FCSTD DOCUMENT  (FreeCAD 1.2R20251223 (Git shallow))
Label: modular-task-light-asm
License: All rights reserved
objects: App::Link×8, App::FeaturePython×8, App::Point×1, Assembly::JointGroup×1, Assembly::AssemblyObject×1
EXTERNAL_REF file=modular-task-light-parts.FCStd obj=Part
EXTERNAL_REF file=modular-task-light-parts.FCStd obj=Body003
EXTERNAL_REF file=modular-task-light-parts.FCStd obj=Body004
EXTERNAL_REF file=modular-task-light-parts.FCStd obj=Part001
EXTERNAL_REF file=modular-task-light-parts.FCStd obj=Part002

FEATURE [App::Point] Origin001  label="Origine"
  Role = Origin
FEATURE [App::Link] lamp_led  label="lamp-led"
  LinkPlacement = pos=(3.28e-14,181.821,89.8213) rot=(1,0,0;1.32331rad)
  LinkedObject = -> <external modular-task-light-parts.FCStd>#Part
  Placement = pos=(3.28e-14,181.821,89.8213) rot=(1,0,0;1.32331rad)
FEATURE [App::Link] Lamp_clip  label="Lamp-clip"
  LinkPlacement = pos=(3.28e-14,181.821,89.8213) rot=(1,0,0;1.32331rad)
  LinkedObject = -> <external modular-task-light-parts.FCStd>#Body003
  Placement = pos=(3.28e-14,181.821,89.8213) rot=(1,0,0;1.32331rad)
FEATURE [App::Link] Arm
  LinkPlacement = pos=(-4.2e-15,132.073,9.84695) rot=(1,0,0;0.784831rad)
  LinkedObject = -> <external modular-task-light-parts.FCStd>#Body004
  Placement = pos=(-4.2e-15,132.073,9.84695) rot=(1,0,0;0.784831rad)
FEATURE [App::FeaturePython] Joint001  label="Fixed001"  # Assembly joint (typed FeaturePython)
  Angle = 0
  AngleMax = 0
  AngleMin = 0
  Detach1 = false
  Detach2 = false
  Distance = 0
  Distance2 = 0
  EnableAngleMax = false
  EnableAngleMin = false
  EnableLengthMax = false
  EnableLengthMin = false
  JointType = 0 (Fixed)
  LengthMax = 0
  LengthMin = 0
  Placement1 = pos=(0,0,0) rot=(1,0,0;3.14159rad)
  Reference1 = -> Assembly [lamp_led.Body.Edge16,lamp_led.Body.Edge16]
  Reference2 = -> Assembly [Lamp_clip.Edge34,Lamp_clip.Edge34]
  Suppressed = false
FEATURE [App::FeaturePython] Joint  label="Revolute003"  # Assembly joint (typed FeaturePython)
  Angle = 0
  AngleMax = 0
  AngleMin = 0
  Detach1 = false
  Detach2 = false
  Distance = 0
  Distance2 = 0
  EnableAngleMax = false
  EnableAngleMin = false
  EnableLengthMax = false
  EnableLengthMin = false
  JointType = 1 (Revolute)
  LengthMax = 0
  LengthMin = 0
  Placement1 = pos=(5,-46.8,3) rot=(0.57735,0.57735,0.57735;2.0944rad)
  Placement2 = pos=(5,50,0) rot=(-0.57735,-0.57735,0.57735;2.0944rad)
  Reference1 = -> Assembly [Lamp_clip.Edge113,Lamp_clip.Edge113]
  Reference2 = -> Assembly [Arm.Edge121,Arm.Edge121]
  Suppressed = false
FEATURE [App::Link] Arm001
  LinkPlacement = pos=(-7e-16,48.3486,-12.7442) rot=(-1,0,0;0.257727rad)
  LinkedObject = -> <external modular-task-light-parts.FCStd>#Body004
  Placement = pos=(-7e-16,48.3486,-12.7442) rot=(-1,0,0;0.257727rad)
FEATURE [App::FeaturePython] Joint002  label="Revolute004"  # Assembly joint (typed FeaturePython)
  Angle = 0
  AngleMax = 0
  AngleMin = 0
  Detach1 = false
  Detach2 = false
  Distance = 0
  Distance2 = 0
  EnableAngleMax = false
  EnableAngleMin = false
  EnableLengthMax = false
  EnableLengthMin = false
  JointType = 1 (Revolute)
  LengthMax = 0
  LengthMin = 0
  Placement1 = pos=(5,-50,0) rot=(-0.57735,-0.57735,0.57735;2.0944rad)
  Placement2 = pos=(5,50,0) rot=(-0.57735,-0.57735,0.57735;2.0944rad)
  Reference1 = -> Assembly [Arm.Edge95,Arm.Edge95]
  Reference2 = -> Assembly [Arm001.Edge121,Arm001.Edge121]
  Suppressed = false
FEATURE [App::Link] Knurling_Nut_Asm  label="Knurling-Nut-Asm"
  LinkedObject = -> <external modular-task-light-parts.FCStd>#Part001
FEATURE [App::Link] Knurling_Nut_Asm001  label="Knurling-Nut-Asm001"
  LinkPlacement = pos=(-1.59e-14,96.6972,-25.4883) rot=(-1,0,0;0.257727rad)
  LinkedObject = -> <external modular-task-light-parts.FCStd>#Part001
  Placement = pos=(-1.59e-14,96.6972,-25.4883) rot=(-1,0,0;0.257727rad)
FEATURE [App::Link] Knurling_Nut_Asm002  label="Knurling-Nut-Asm002"
  LinkPlacement = pos=(4.6e-15,167.448,45.1822) rot=(1,0,0;0.784831rad)
  LinkedObject = -> <external modular-task-light-parts.FCStd>#Part001
  Placement = pos=(4.6e-15,167.448,45.1822) rot=(1,0,0;0.784831rad)
FEATURE [App::FeaturePython] Joint004  label="Fixed002"  # Assembly joint (typed FeaturePython)
  Angle = 0
  AngleMax = 0
  AngleMin = 0
  Detach1 = false
  Detach2 = false
  Distance = 0
  Distance2 = 0
  EnableAngleMax = false
  EnableAngleMin = false
  EnableLengthMax = false
  EnableLengthMin = false
  JointType = 0 (Fixed)
  LengthMax = 0
  LengthMin = 0
  Placement1 = pos=(-3.5,0,0) rot=(0.57735,0.57735,0.57735;2.0944rad)
  Placement2 = pos=(8,50,0) rot=(0.57735,0.57735,0.57735;2.0944rad)
  Reference1 = -> Assembly [Knurling_Nut_Asm002.Link.Edge254,Knurling_Nut_Asm002.Link.Edge254]
  Reference2 = -> Assembly [Arm.Edge112,Arm.Edge112]
  Suppressed = false
FEATURE [App::FeaturePython] Joint005  label="Fixed003"  # Assembly joint (typed FeaturePython)
  Angle = 0
  AngleMax = 0
  AngleMin = 0
  Detach1 = false
  Detach2 = false
  Distance = 0
  Distance2 = 0
  EnableAngleMax = false
  EnableAngleMin = false
  EnableLengthMax = false
  EnableLengthMin = false
  JointType = 0 (Fixed)
  LengthMax = 0
  LengthMin = 0
  Placement1 = pos=(-3.5,0,0) rot=(0.57735,0.57735,0.57735;2.0944rad)
  Placement2 = pos=(8,50,-3.6e-15) rot=(0.57735,0.57735,0.57735;2.0944rad)
  Reference1 = -> Assembly [Knurling_Nut_Asm001.Link.Edge254,Knurling_Nut_Asm001.Link.Edge254]
  Reference2 = -> Assembly [Arm001.Edge112,Arm001.Edge112]
  Suppressed = false
FEATURE [App::Link] _2020_Support_Asm  label="2020-Support-Asm"
  LinkedObject = -> <external modular-task-light-parts.FCStd>#Part002
FEATURE [App::FeaturePython] GroundedJoint  label="GroundedJoint003"  # Assembly grounded joint (typed FeaturePython)
  ObjectToGround = -> _2020_Support_Asm
FEATURE [App::FeaturePython] Joint006  label="Revolute007"  # Assembly joint (typed FeaturePython)
  Angle = 0
  AngleMax = 0
  AngleMin = 0
  Detach1 = false
  Detach2 = false
  Distance = 0
  Distance2 = 0
  EnableAngleMax = false
  EnableAngleMin = false
  EnableLengthMax = false
  EnableLengthMin = false
  JointType = 1 (Revolute)
  LengthMax = 0
  LengthMin = 0
  Placement1 = pos=(-5,-50,3e-15) rot=(-0.57735,-0.57735,0.57735;2.0944rad)
  Placement2 = pos=(-5,0,0) rot=(-0.57735,-0.57735,0.57735;2.0944rad)
  Reference1 = -> Assembly [Arm001.Edge1,Arm001.Edge1]
  Reference2 = -> Assembly [_2020_Support_Asm.Body005.Edge55,_2020_Support_Asm.Body005.Edge55]
  Suppressed = false
FEATURE [App::FeaturePython] Joint007  label="Fixed005"  # Assembly joint (typed FeaturePython)
  Angle = 0
  AngleMax = 0
  AngleMin = 0
  Detach1 = false
  Detach2 = false
  Distance = 0
  Distance2 = 0
  EnableAngleMax = false
  EnableAngleMin = false
  EnableLengthMax = false
  EnableLengthMin = false
  JointType = 0 (Fixed)
  LengthMax = 0
  LengthMin = 0
  Placement1 = pos=(-3.5,0,0) rot=(0.57735,0.57735,0.57735;2.0944rad)
  Placement2 = pos=(8,0,0) rot=(0.57735,0.57735,0.57735;2.0944rad)
  Reference1 = -> Assembly [Knurling_Nut_Asm.Link.Edge254,Knurling_Nut_Asm.Link.Edge254]
  Reference2 = -> Assembly [_2020_Support_Asm.Body005.Edge59,_2020_Support_Asm.Body005.Edge59]
  Suppressed = false
FEATURE [Assembly::JointGroup] Joints
  Group = -> [Joint001,Joint,Joint002,Joint004,Joint005,GroundedJoint,Joint006,Joint007]
FEATURE [Assembly::AssemblyObject] Assembly  label="modular-task-light"
  Group = -> [Joints,lamp_led,Lamp_clip,Arm,Joint001,Joint,Arm001,Joint002,Knurling_Nut_Asm,Knurling_Nut_Asm001,Knurling_Nut_Asm002,Joint004,Joint005,_2020_Support_Asm,GroundedJoint,Joint006,Joint007]
  Origin = -> Origin
  Type = Assembly

RESOLVED EXTERNAL PARTS (link-assembly join: the EXTERNAL_REF files above that resolve inside this repo's crawl, each included once):
---- part modular-task-light-parts.FCStd = doc fcstd_f716f1105b3c ----
FCSTD DOCUMENT  (FreeCAD 1.2R20251223 (Git shallow))
Label: modular-task-light-parts
License: All rights reserved
objects: Sketcher::SketchObject×27, PartDesign::Chamfer×22, PartDesign::Pocket×15, PartDesign::Pad×11, App::Point×10, PartDesign::Body×7, PartDesign::Fillet×7, Part::FeaturePython×5, App::Part×3, PartDesign::Mirrored×3, App::DocumentObjectGroup×2, PartDesign::Revolution×1, PartDesign::AdditivePipe×1, PartDesign::LinearPattern×1, PartDesign::Draft×1, PartDesign::PolarPattern×1, App::Link×1, App::VarSet×1
note: 250 computed .brp shape members not serialized (recipe doc carries the construction recipe); baked Part::Feature solids carry a one-line shape summary decoded from their .brp

FEATURE [App::Point] Origin001  label="Origine"
  Role = Origin
FEATURE [Sketcher::SketchObject] Sketch
  ArcFitTolerance = 1e-06
  AttachmentSupport = -> [Origin]
  ExternalTypes = [0]
  FullyConstrained = true
  MakeInternals = false
  MapMode = 5
  Placement = pos=(0,0,0) rot=(1,0,0;1.5708rad)
  sketch-geometry (6):
    g0: LineSegment StartX=0 StartY=0 StartZ=0 EndX=29.6 EndY=0 EndZ=0
    g1: LineSegment StartX=29.6 StartY=0 StartZ=0 EndX=29.6 EndY=7.7 EndZ=0
    g2: LineSegment StartX=29.6 StartY=7.7 StartZ=0 EndX=23.5 EndY=7.7 EndZ=0
    g3: LineSegment StartX=23.5 StartY=7.7 StartZ=0 EndX=23.5 EndY=6.2 EndZ=0
    g4: LineSegment StartX=23.5 StartY=6.2 StartZ=0 EndX=0 EndY=6.2 EndZ=0
    g5: LineSegment StartX=0 StartY=6.2 StartZ=0 EndX=0 EndY=0 EndZ=0
  constraints (17):
    c: Coincident(g-1,g0)
    c: PointOnObject(g0,g-1)
    c: Coincident(g0,g1)
    c: Vertical(g1)
    c: Coincident(g1,g2)
    c: Horizontal(g2)
    c: Coincident(g2,g3)
    c: Vertical(g3)
    c: Coincident(g3,g4)
    c: Horizontal(g4)
    c: Coincident(g4,g5)
    c: Coincident(g5,g0)
    c: Vertical(g5)
    c: DistanceX(g0,g0) = 29.6
    c: Distance(g-2,g3) = 23.5
    c: DistanceY(g1,g1) = 7.7
    c: Distance(g3,g3) = 1.5
FEATURE [PartDesign::Revolution] Revolution
  Angle = 360
  Angle2 = 0
  Axis = (0,2e-16,1)
  Base = (0,0,0)
  FuseOrder = 0
  Profile = -> Sketch
  ReferenceAxis = -> Sketch [V_Axis]
  Refine = true
  Reversed = true
  Suppressed = false
  Type = 0
FEATURE [PartDesign::Chamfer] Chamfer
  Angle = 45
  Base = -> Revolution [Edge4]
  BaseFeature = -> Revolution
  ChamferType = 0
  FlipDirection = false
  Refine = true
  Size = 1
  Size2 = 1
  SupportTransform = false
  Suppressed = false
  UseAllEdges = false
FEATURE [Sketcher::SketchObject] Sketch001
  ArcFitTolerance = 1e-06
  AttachmentSupport = -> [Origin]
  ExternalTypes = [0]
  FullyConstrained = true
  MakeInternals = false
  MapMode = 5
  sketch-geometry (3):
    g0: Circle CenterX=0 CenterY=0 CenterZ=0 NormalX=0 NormalY=0 NormalZ=1 AngleXU=0 Radius=2.25
    g1: Circle CenterX=14 CenterY=0 CenterZ=0 NormalX=0 NormalY=0 NormalZ=1 AngleXU=0 Radius=1.95
    g2: Circle CenterX=-14 CenterY=0 CenterZ=0 NormalX=0 NormalY=0 NormalZ=1 AngleXU=0 Radius=1.95
  constraints (7):
    c: Coincident(g0,g-1)
    c: PointOnObject(g1,g-1)
    c: Equal(g2,g1)
    c: Symmetric(g2,g1,g-2)
    c: Diameter(g0) = 4.5
    c: Diameter(g1) = 3.9
    c: DistanceX(g2,g1) = 28
FEATURE [PartDesign::Pocket] Pocket
  BaseFeature = -> Chamfer
  Direction = (0,0,-1)
  Length = 2
  Length2 = 5
  Profile = -> Sketch001
  ReferenceAxis = -> Sketch001 [N_Axis]
  Refine = true
  Reversed = true
  SideType = 0
  Suppressed = false
  Type = 0
  Type2 = 0
FEATURE [PartDesign::Chamfer] Chamfer001
  Angle = 45
  Base = -> Pocket [Edge2,Edge5]
  BaseFeature = -> Pocket
  ChamferType = 0
  FlipDirection = false
  Refine = true
  Size = 0.5
  Size2 = 1
  SupportTransform = false
  Suppressed = false
  UseAllEdges = false
FEATURE [Sketcher::SketchObject] Sketch002
  ArcFitTolerance = 1e-06
  AttachmentSupport = -> [Origin]
  ExternalGeometry = -> [Chamfer001]
  ExternalTypes = [0]
  FullyConstrained = true
  MakeInternals = false
  MapMode = 5
  sketch-geometry (4):
    g0: ArcOfCircle CenterX=0 CenterY=-22.1 CenterZ=0 NormalX=0 NormalY=0 NormalZ=1 AngleXU=0 Radius=2 StartAngle=-9e-16 EndAngle=3.14159
    g1: ArcOfCircle CenterX=0 CenterY=-31.1 CenterZ=0 NormalX=0 NormalY=0 NormalZ=1 AngleXU=0 Radius=2 StartAngle=3.14159 EndAngle=6.28319
    g2: LineSegment StartX=2 StartY=-22.1 StartZ=0 EndX=2 EndY=-31.1 EndZ=0
    g3: LineSegment StartX=-2 StartY=-22.1 StartZ=0 EndX=-2 EndY=-31.1 EndZ=0
  constraints (10):
    c: Tangent(g0,g2) = 1.5708
    c: Tangent(g0,g3) = -1.5708
    c: Tangent(g1,g2) = 1.5708
    c: Tangent(g1,g3) = -1.5708
    c: Equal(g0,g1)
    c: PointOnObject(g0,g-2)
    c: PointOnObject(g1,g-2)
    c: Distance(g1,g1) = 4
    c: Distance(g0,g-3) = 7
    c: Tangent(g1,g-3)
FEATURE [PartDesign::Pocket] Pocket001
  BaseFeature = -> Chamfer001
  Direction = (0,0,-1)
  Length = 3
  Length2 = 5
  Profile = -> Sketch002
  ReferenceAxis = -> Sketch002 [N_Axis]
  Refine = true
  Reversed = true
  SideType = 0
  Suppressed = false
  Type = 0
  Type2 = 0
FEATURE [PartDesign::Body] Body  label="lamp-led-body"
  AllowCompound = true
  Group = -> [Sketch,Revolution,Chamfer,Sketch001,Pocket,Chamfer001,Sketch002,Pocket001]
  Origin = -> Origin
  Tip = -> Pocket001
FEATURE [App::Point] Origin003  label="Origine002"
  Role = Origin
FEATURE [Sketcher::SketchObject] Sketch003
  ArcFitTolerance = 1e-06
  AttachmentSupport = -> [Origin002]
  ExternalTypes = [0]
  FullyConstrained = true
  MakeInternals = false
  MapMode = 5
  sketch-geometry (1):
    g0: Circle CenterX=0 CenterY=0 CenterZ=0 NormalX=0 NormalY=0 NormalZ=1 AngleXU=0 Radius=25
  constraints (2):
    c: Coincident(g0,g-1)
    c: Diameter(g0) = 50
FEATURE [PartDesign::Pad] Pad
  Direction = (0,0,1)
  Length = 1
  Length2 = 10
  Profile = -> Sketch003
  ReferenceAxis = -> Sketch003 [N_Axis]
  Refine = true
  SideType = 0
  Suppressed = false
  Type = 0
  Type2 = 0
FEATURE [PartDesign::Body] Body001  label="lamp-led-diffuser"
  AllowCompound = true
  Group = -> [Sketch003,Pad]
  Origin = -> Origin002
  Placement = pos=(-9e-16,2.7e-15,5.45) rot=(0,0,1;3.14159rad)
  Tip = -> Pad
FEATURE [App::Point] Origin005  label="Origine004"
  Role = Origin
FEATURE [Sketcher::SketchObject] Sketch004
  ArcFitTolerance = 1e-06
  AttachmentSupport = -> [Origin004]
  ExternalTypes = [0]
  FullyConstrained = true
  MakeInternals = false
  MapMode = 5
  Placement = pos=(0,0,0) rot=(1,0,0;1.5708rad)
  sketch-geometry (1):
    g0: Circle CenterX=0 CenterY=0 CenterZ=0 NormalX=0 NormalY=0 NormalZ=1 AngleXU=0 Radius=1.475
  constraints (2):
    c: Coincident(g0,g-1)
    c: Diameter(g0) = 2.95
FEATURE [PartDesign::Pad] Pad001
  Direction = (0,-1,2e-16)
  Length = 15
  Length2 = 10
  Profile = -> Sketch004
  ReferenceAxis = -> Sketch004 [N_Axis]
  Refine = true
  SideType = 0
  Suppressed = false
  Type = 0
  Type2 = 0
FEATURE [PartDesign::Body] Body002  label="lamp-led-cable"
  AllowCompound = true
  Group = -> [Sketch004,Pad001]
  Origin = -> Origin004
  Placement = pos=(0,-20,1.5) rot=(0,0,1;0rad)
  Tip = -> Pad001
FEATURE [App::Part] Part  label="lamp-led"
  Group = -> [Body,Body001,Body002]
  Origin = -> Origin006
FEATURE [App::Point] Origin007  label="Origine006"
  Role = Origin
FEATURE [App::Point] Origin009  label="Origine008"
  Role = Origin
FEATURE [Sketcher::SketchObject] Sketch005
  ArcFitTolerance = 1e-06
  AttachmentSupport = -> [Origin008]
  ExternalTypes = [0]
  FullyConstrained = true
  MakeInternals = false
  MapMode = 5
  sketch-geometry (2):
    g0: Circle CenterX=0 CenterY=0 CenterZ=0 NormalX=0 NormalY=0 NormalZ=1 AngleXU=0 Radius=29.8
    g1: Circle CenterX=0 CenterY=0 CenterZ=0 NormalX=0 NormalY=0 NormalZ=1 AngleXU=0 Radius=31.8
  constraints (4):
    c: Coincident(g0,g-1)
    c: Diameter(g0) = 59.6
    c: Coincident(g1,g0)
    c: Distance(g0,g1) = 2
FEATURE [PartDesign::Pad] Pad002
  Direction = (0,0,1)
  Length = 8
  Length2 = 10
  Profile = -> Sketch005
  ReferenceAxis = -> Sketch005 [N_Axis]
  Refine = true
  SideType = 0
  Suppressed = false
  Type = 0
  Type2 = 0
FEATURE [Sketcher::SketchObject] Sketch008
  ArcFitTolerance = 1e-06
  AttachmentSupport = -> [Origin008]
  ExternalGeometry = -> [Pad002]
  ExternalTypes = [0]
  FullyConstrained = true
  MakeInternals = false
  MapMode = 5
  sketch-geometry (1):
    g0: Circle CenterX=0 CenterY=0 CenterZ=0 NormalX=0 NormalY=0 NormalZ=1 AngleXU=0 Radius=31.8
  constraints (2):
    c: Coincident(g0,g-1)
    c: Equal(g-3,g0)
FEATURE [PartDesign::Pad] Pad003
  BaseFeature = -> Pad002
  Direction = (0,0,1)
  Length = 2
  Length2 = 10
  Profile = -> Sketch008
  ReferenceAxis = -> Sketch008 [N_Axis]
  Refine = true
  Reversed = true
  SideType = 0
  Suppressed = false
  Type = 0
  Type2 = 0
FEATURE [Sketcher::SketchObject] Sketch009
  ArcFitTolerance = 1e-06
  AttachmentSupport = -> [Origin008]
  ExternalTypes = [0]
  FullyConstrained = true
  MakeInternals = false
  MapMode = 5
  Placement = pos=(0,0,0) rot=(0.57735,0.57735,0.57735;2.0944rad)
  sketch-geometry (8):
    g0: LineSegment StartX=-7 StartY=0 StartZ=0 EndX=-5 EndY=0 EndZ=0
    g1: LineSegment StartX=-5 StartY=0 StartZ=0 EndX=-5 EndY=10 EndZ=0
    g2: LineSegment StartX=-5 StartY=10 StartZ=0 EndX=-7 EndY=10 EndZ=0
    g3: LineSegment StartX=-7 StartY=10 StartZ=0 EndX=-7 EndY=0 EndZ=0
    g4: LineSegment StartX=5 StartY=0 StartZ=0 EndX=7 EndY=0 EndZ=0
    g5: LineSegment StartX=7 StartY=0 StartZ=0 EndX=7 EndY=10 EndZ=0
    g6: LineSegment StartX=7 StartY=10 StartZ=0 EndX=5 EndY=10 EndZ=0
    g7: LineSegment StartX=5 StartY=10 StartZ=0 EndX=5 EndY=0 EndZ=0
  constraints (23):
    c: Coincident(g0,g1)
    c: Coincident(g1,g2)
    c: Coincident(g2,g3)
    c: Coincident(g3,g0)
    c: Horizontal(g0)
    c: Horizontal(g2)
    c: Vertical(g1)
    c: Vertical(g3)
    c: PointOnObject(g0,g-1)
    c: Coincident(g4,g5)
    c: Coincident(g5,g6)
    c: Coincident(g6,g7)
    c: Coincident(g7,g4)
    c: Horizontal(g4)
    c: Horizontal(g6)
    c: Vertical(g5)
    c: Vertical(g7)
    c: PointOnObject(g4,g-1)
    c: Equal(g6,g2)
    c: Symmetric(g1,g6,g-2)
    c: Distance(g6,g6) = 2
    c: Distance(g1,g6) = 10
    c: Distance(g5,g5) = 10
FEATURE [PartDesign::Pocket] Pocket003
  BaseFeature = -> Pad003
  Direction = (-1,0,0)
  Length = 5
  Length2 = 5
  Profile = -> Sketch009
  ReferenceAxis = -> Sketch009 [N_Axis]
  Refine = true
  SideType = 2
  Suppressed = false
  Type = 1
  Type2 = 0
FEATURE [PartDesign::Pad] Pad004
  BaseFeature = -> Pocket003
  Direction = (0,0,1)
  Length = 1
  Length2 = 10
  Profile = -> Pocket003 [Face10,Face1]
  Refine = true
  SideType = 0
  Suppressed = false
  Type = 0
  Type2 = 0
FEATURE [Sketcher::SketchObject] Sketch010
  ArcFitTolerance = 1e-06
  AttachmentSupport = -> [Pad004]
  ExternalTypes = [0,0]
  FullyConstrained = true
  MakeInternals = false
  MapMode = 5
  Placement = pos=(0,5,0) rot=(0,0.707107,0.707107;3.14159rad)
  sketch-geometry (4):
    g0: LineSegment StartX=29.3775 StartY=9 StartZ=0 EndX=28.3775 EndY=9 EndZ=0
    g1: LineSegment StartX=28.3775 StartY=9 StartZ=0 EndX=28.3775 EndY=8 EndZ=0
    g2: LineSegment StartX=28.3775 StartY=8 StartZ=0 EndX=29.3775 EndY=7.2 EndZ=0
    g3: LineSegment StartX=29.3775 StartY=7.2 StartZ=0 EndX=29.3775 EndY=9 EndZ=0
  constraints (12):
    c: Horizontal(g0)
    c: Coincident(g0,g1)
    c: Vertical(g1)
    c: Coincident(g1,g2)
    c: PointOnObject(g2,g-3)
    c: Coincident(g2,g3)
    c: Coincident(g3,g0)
    c: DistanceX(g0,g0) = 1
    c: DistanceY(g1,g1) = 1
    c: DistanceY(g3,g3) = 1.8
    c: PointOnObject(g0,g-3)
    c: Distance(g-1,g0) = 9
FEATURE [PartDesign::AdditivePipe] AdditivePipe
  AuxiliaryCurvilinear = true
  AuxiliarySpineTangent = false
  BaseFeature = -> Pad004
  Binormal = (0,0,0)
  Mode = 1
  Profile = -> Sketch010
  Refine = true
  Spine = -> Pad004 [Edge2]
  SpineTangent = false
  Suppressed = false
  Transformation = 0
  Transition = 0
FEATURE [Sketcher::SketchObject] Sketch011
  ArcFitTolerance = 1e-06
  AttachmentSupport = -> [Origin008]
  ExternalGeometry = -> [AdditivePipe]
  ExternalTypes = [0]
  FullyConstrained = true
  MakeInternals = false
  MapMode = 5
  Placement = pos=(0,0,0) rot=(1,0,0;1.5708rad)
  sketch-geometry (5):
    g0: LineSegment StartX=0 StartY=0 StartZ=0 EndX=-30.3 EndY=0 EndZ=0
    g1: LineSegment StartX=-30.3 StartY=0 StartZ=0 EndX=-30.3 EndY=1 EndZ=0
    g2: LineSegment StartX=-30.3 StartY=1 StartZ=0 EndX=-27.3 EndY=4 EndZ=0
    g3: LineSegment StartX=-27.3 StartY=4 StartZ=0 EndX=0 EndY=4 EndZ=0
    g4: LineSegment StartX=0 StartY=4 StartZ=0 EndX=0 EndY=0 EndZ=0
  constraints (14):
    c: Coincident(g-1,g0)
    c: PointOnObject(g0,g-1)
    c: Coincident(g0,g1)
    c: Vertical(g1)
    c: Coincident(g1,g2)
    c: Coincident(g2,g3)
    c: Horizontal(g3)
    c: Coincident(g3,g4)
    c: Coincident(g4,g0)
    c: Vertical(g4)
    c: Distance(g1,g1) = 1
    c: Distance(g4,g4) = 4
    c: Angle(g2,g1) = 0.785398
    c: Distance(g-3,g1) = 1.5
FEATURE [PartDesign::Pocket] Pocket004
  BaseFeature = -> AdditivePipe
  Direction = (0,1,-2e-16)
  Length = 11
  Length2 = 5
  Profile = -> Sketch011
  ReferenceAxis = -> Sketch011 [N_Axis]
  Refine = true
  SideType = 2
  Suppressed = false
  Type = 0
  Type2 = 0
FEATURE [PartDesign::Mirrored] Mirrored
  BaseFeature = -> Pocket004
  MirrorPlane = -> Sketch011 [V_Axis]
  Originals = -> [Pocket004,AdditivePipe]
  Refine = true
  Suppressed = false
  TransformMode = 0
FEATURE [PartDesign::Fillet] Fillet
  Base = -> Mirrored [Edge1,Edge3,Edge69,Edge57]
  BaseFeature = -> Mirrored
  Radius = 0.4
  Refine = true
  SupportTransform = false
  Suppressed = false
  UseAllEdges = false
FEATURE [PartDesign::Fillet] Fillet001
  Base = -> Fillet [Edge77,Edge58,Edge55,Edge80]
  BaseFeature = -> Fillet
  Radius = 2
  Refine = true
  SupportTransform = false
  Suppressed = false
  UseAllEdges = false
FEATURE [PartDesign::Chamfer] Chamfer002
  Angle = 45
  Base = -> Fillet001 [Edge21,Edge7]
  BaseFeature = -> Fillet001
  ChamferType = 0
  FlipDirection = false
  Refine = true
  Size = 1
  Size2 = 1
  SupportTransform = false
  Suppressed = false
  UseAllEdges = false
FEATURE [PartDesign::Fillet] Fillet003
  Base = -> Chamfer002 [Edge39,Edge41,Edge45,Edge28]
  BaseFeature = -> Chamfer002
  Radius = 1
  Refine = true
  SupportTransform = false
  Suppressed = false
  UseAllEdges = false
FEATURE [Sketcher::SketchObject] Sketch012
  ArcFitTolerance = 1e-06
  AttachmentSupport = -> [Origin008]
  ExternalTypes = [0]
  FullyConstrained = true
  MakeInternals = false
  MapMode = 5
  sketch-geometry (4):
    g0: LineSegment StartX=-5 StartY=-31.4045 StartZ=0 EndX=-5 EndY=-51.8 EndZ=0
    g1: LineSegment StartX=-5 StartY=-51.8 StartZ=0 EndX=5 EndY=-51.8 EndZ=0
    g2: LineSegment StartX=5 StartY=-51.8 StartZ=0 EndX=5 EndY=-31.4045 EndZ=0
    g3: LineSegment StartX=5 StartY=-31.4045 StartZ=0 EndX=-5 EndY=-31.4045 EndZ=0
  constraints (12):
    c: Coincident(g0,g1)
    c: Coincident(g1,g2)
    c: Coincident(g2,g3)
    c: Coincident(g3,g0)
    c: Vertical(g0)
    c: Vertical(g2)
    c: Horizontal(g1)
    c: Horizontal(g3)
    c: PointOnObject(g0,g-3)
    c: PointOnObject(g2,g-3)
    c: Distance(g1,g1) = 10
    c: Distance(g-3,g1) = 20
FEATURE [PartDesign::Pad] Pad005
  BaseFeature = -> Fillet003
  Direction = (0,0,1)
  Length = 8
  Length2 = 2
  Profile = -> Sketch012
  ReferenceAxis = -> Sketch012 [N_Axis]
  Refine = true
  SideType = 1
  Suppressed = false
  Type = 0
  Type2 = 0
FEATURE [PartDesign::Fillet] Fillet004
  Base = -> Pad005 [Edge115]
  BaseFeature = -> Pad005
  Radius = 5
  Refine = true
  SupportTransform = false
  Suppressed = false
  UseAllEdges = false
FEATURE [PartDesign::Chamfer] Chamfer003
  Angle = 45
  Base = -> Fillet004 [Edge51]
  BaseFeature = -> Fillet004
  ChamferType = 0
  FlipDirection = false
  Refine = true
  Size = 1
  Size2 = 1
  SupportTransform = false
  Suppressed = false
  UseAllEdges = false
FEATURE [PartDesign::Fillet] Fillet005
  Base = -> Chamfer003 [Edge47,Edge6]
  BaseFeature = -> Chamfer003
  Radius = 2
  Refine = true
  SupportTransform = false
  Suppressed = false
  UseAllEdges = false
FEATURE [Sketcher::SketchObject] Sketch013
  ArcFitTolerance = 1e-06
  AttachmentSupport = -> [Origin008]
  ExternalTypes = [0]
  FullyConstrained = true
  MakeInternals = false
  MapMode = 5
  sketch-geometry (1):
    g0: Circle CenterX=0 CenterY=0 CenterZ=0 NormalX=0 NormalY=0 NormalZ=1 AngleXU=0 Radius=25
  constraints (2):
    c: Coincident(g0,g-1)
    c: Diameter(g0) = 50
FEATURE [PartDesign::Pocket] Pocket005
  BaseFeature = -> Fillet005
  Direction = (0,0,-1)
  Length = 5
  Length2 = 5
  Profile = -> Sketch013
  ReferenceAxis = -> Sketch013 [N_Axis]
  Refine = true
  SideType = 0
  Suppressed = false
  Type = 0
  Type2 = 0
FEATURE [Sketcher::SketchObject] Sketch014
  ArcFitTolerance = 1e-06
  AttachmentSupport = -> [Origin008]
  ExternalGeometry = -> [Pocket005]
  ExternalTypes = [0]
  FullyConstrained = true
  MakeInternals = false
  MapMode = 5
  Placement = pos=(0,0,0) rot=(1,0,0;1.5708rad)
  sketch-geometry (6):
    g0: ArcOfCircle CenterX=0 CenterY=-1.32361 CenterZ=0 NormalX=0 NormalY=0 NormalZ=1 AngleXU=0 Radius=1.6 StartAngle=3.14159 EndAngle=6.28319
    g1: ArcOfCircle CenterX=0 CenterY=1.5 CenterZ=0 NormalX=0 NormalY=0 NormalZ=1 AngleXU=0 Radius=1.6 StartAngle=0 EndAngle=3.14159
    g2: LineSegment StartX=-1.6 StartY=-1.32361 StartZ=0 EndX=-1.6 EndY=1.5 EndZ=0
    g3: LineSegment StartX=1.6 StartY=-1.32361 StartZ=0 EndX=1.6 EndY=1.5 EndZ=0
    g4: GeomPoint X=1.45 Y=-2 Z=0
    g5: GeomPoint X=-1.45 Y=-2 Z=0
  constraints (15):
    c: Tangent(g0,g2) = 1.5708
    c: Tangent(g0,g3) = -1.5708
    c: Tangent(g1,g2) = 1.5708
    c: Tangent(g1,g3) = -1.5708
    c: Equal(g0,g1)
    c: PointOnObject(g0,g-2)
    c: PointOnObject(g1,g-2)
    c: Distance(g1,g-1) = 1.5
    c: Distance(g1,g1) = 3.2
    c: PointOnObject(g4,g-3)
    c: PointOnObject(g5,g-3)
    c: PointOnObject(g4,g0)
    c: PointOnObject(g5,g0)
    c: Distance(g5,g4) = 2.9
    c: Distance(g1,g-3) = 3.5
FEATURE [PartDesign::Pocket] Pocket006
  BaseFeature = -> Pocket005
  Direction = (0,1,-2e-16)
  Length = 5
  Length2 = 5
  Profile = -> Sketch014
  ReferenceAxis = -> Sketch014 [N_Axis]
  Refine = true
  Reversed = true
  SideType = 0
  Suppressed = false
  Type = 1
  Type2 = 0
FEATURE [Sketcher::SketchObject] Sketch015
  ArcFitTolerance = 1e-06
  AttachmentSupport = -> [Origin008]
  ExternalGeometry = -> [Pocket006]
  ExternalTypes = [0]
  FullyConstrained = true
  MakeInternals = false
  MapMode = 5
  Placement = pos=(0,0,0) rot=(0.57735,0.57735,0.57735;2.0944rad)
  sketch-geometry (2):
    g0: Circle CenterX=-46.8 CenterY=3 CenterZ=0 NormalX=0 NormalY=0 NormalZ=1 AngleXU=0 Radius=2.5
    g1: Circle [constr] CenterX=-46.8 CenterY=3 CenterZ=0 NormalX=0 NormalY=0 NormalZ=1 AngleXU=0 Radius=1.7
  constraints (4):
    c: Coincident(g0,g-3)
    c: Coincident(g1,g0)
    c: Diameter(g1) = 3.4
    c: Distance(g1,g0) = 0.8
FEATURE [PartDesign::Pad] Pad006
  BaseFeature = -> Pocket006
  Direction = (1,0,0)
  Length = 10
  Length2 = 10
  Profile = -> Sketch015
  ReferenceAxis = -> Sketch015 [N_Axis]
  Refine = true
  SideType = 2
  Suppressed = false
  Type = 0
  Type2 = 0
FEATURE [Sketcher::SketchObject] Sketch016
  ArcFitTolerance = 1e-06
  AttachmentSupport = -> [Origin008]
  ExternalGeometry = -> [Pad006]
  ExternalTypes = [0]
  FullyConstrained = true
  MakeInternals = false
  MapMode = 5
  Placement = pos=(0,0,0) rot=(0.57735,0.57735,0.57735;2.0944rad)
  sketch-geometry (1):
    g0: Circle CenterX=-46.8 CenterY=3 CenterZ=0 NormalX=0 NormalY=0 NormalZ=1 AngleXU=0 Radius=1.7
  constraints (2):
    c: Coincident(g0,g-3)
    c: Diameter(g0) = 3.4
FEATURE [PartDesign::Pocket] Pocket007
  BaseFeature = -> Pad006
  Direction = (-1,0,0)
  Length = 5
  Length2 = 5
  Profile = -> Sketch016
  ReferenceAxis = -> Sketch016 [N_Axis]
  Refine = true
  SideType = 2
  Suppressed = false
  Type = 1
  Type2 = 0
FEATURE [PartDesign::Chamfer] Chamfer004
  Angle = 45
  Base = -> Pocket007 [Edge68,Edge49]
  BaseFeature = -> Pocket007
  ChamferType = 0
  FlipDirection = false
  Refine = true
  Size = 0.6
  Size2 = 1
  SupportTransform = false
  Suppressed = false
  UseAllEdges = false
FEATURE [PartDesign::Fillet] Fillet006
  Base = -> Chamfer004 [Edge70,Edge72]
  BaseFeature = -> Chamfer004
  Radius = 3
  Refine = true
  SupportTransform = false
  Suppressed = false
  UseAllEdges = false
FEATURE [PartDesign::Chamfer] Chamfer005
  Angle = 45
  Base = -> Fillet006 [Edge14]
  BaseFeature = -> Fillet006
  ChamferType = 0
  FlipDirection = false
  Refine = true
  Size = 0.8
  Size2 = 1
  SupportTransform = false
  Suppressed = false
  UseAllEdges = false
FEATURE [PartDesign::Body] Body003  label="Lamp-clip"
  AllowCompound = true
  Group = -> [Sketch005,Pad002,Sketch008,Pad003,Sketch009,Pocket003,Pad004,Sketch010,AdditivePipe,Sketch011,Pocket004,Mirrored,Fillet,Fillet001,Chamfer002,Fillet003,Sketch012,Pad005,Fillet004,Chamfer003,Fillet005,Sketch013,Pocket005,Sketch014,Pocket006,Sketch015,Pad006,Sketch016,Pocket007,Chamfer004,Fillet006,Chamfer005]
  Origin = -> Origin008
  Tip = -> Chamfer005
FEATURE [App::Point] Origin011  label="Origine010"
  Role = Origin
FEATURE [Sketcher::SketchObject] Sketch017
  ArcFitTolerance = 1e-06
  AttachmentSupport = -> [Origin010]
  ExternalTypes = [0]
  FullyConstrained = true
  MakeInternals = false
  MapMode = 5
  Placement = pos=(0,0,0) rot=(0.57735,0.57735,0.57735;2.0944rad)
  expr: Constraints[10] = VarSet.arm_length
  sketch-geometry (8):
    g0: LineSegment StartX=-55 StartY=0 StartZ=0 EndX=-55 EndY=-5 EndZ=0
    g1: LineSegment StartX=-55 StartY=-5 StartZ=0 EndX=55 EndY=-5 EndZ=0
    g2: LineSegment StartX=55 StartY=-5 StartZ=0 EndX=55 EndY=0 EndZ=0
    g3: ArcOfCircle CenterX=-50 CenterY=0 CenterZ=0 NormalX=0 NormalY=0 NormalZ=1 AngleXU=0 Radius=5 StartAngle=1.5708 EndAngle=3.14159
    g4: ArcOfCircle CenterX=50 CenterY=0 CenterZ=0 NormalX=0 NormalY=0 NormalZ=1 AngleXU=0 Radius=5 StartAngle=0 EndAngle=1.5708
    g5: LineSegment StartX=50 StartY=5 StartZ=0 EndX=-50 EndY=5 EndZ=0
    g6: Circle CenterX=50 CenterY=0 CenterZ=0 NormalX=0 NormalY=0 NormalZ=1 AngleXU=0 Radius=1.7
    g7: Circle CenterX=-50 CenterY=0 CenterZ=0 NormalX=0 NormalY=0 NormalZ=1 AngleXU=0 Radius=1.7
  constraints (20):
    c: PointOnObject(g0,g-1)
    c: Vertical(g0)
    c: Coincident(g0,g1)
    c: Horizontal(g1)
    c: Coincident(g1,g2)
    c: PointOnObject(g3,g-1)
    c: Coincident(g3,g0)
    c: Horizontal(g5)
    c: Tangent(g3,g1)
    c: Distance(g4,g1) = 10
    c: DistanceX(g3,g4) = 100
    c: Coincident(g6,g4)
    c: Coincident(g7,g3)
    c: Tangent(g5,g3) = -1.5708
    c: Equal(g6,g7)
    c: Diameter(g7) = 3.4
    c: Tangent(g4,g2) = -1.5708
    c: Vertical(g2)
    c: Tangent(g5,g4) = -1.5708
    c: Symmetric(g4,g3,g-2)
FEATURE [PartDesign::Pad] Pad007
  Direction = (1,0,0)
  Length = 16
  Length2 = 10
  Profile = -> Sketch017
  ReferenceAxis = -> Sketch017 [N_Axis]
  Refine = true
  SideType = 2
  Suppressed = false
  Type = 0
  Type2 = 0
FEATURE [Sketcher::SketchObject] Sketch018
  ArcFitTolerance = 1e-06
  AttachmentSupport = -> [Origin010]
  ExternalGeometry = -> [Pad007]
  ExternalTypes = [0,0]
  FullyConstrained = true
  MakeInternals = false
  MapMode = 5
  Placement = pos=(0,0,0) rot=(0.57735,0.57735,0.57735;2.0944rad)
  sketch-geometry (5):
    g0: LineSegment StartX=42.5 StartY=-5 StartZ=0 EndX=57.5 EndY=-5 EndZ=0
    g1: LineSegment StartX=57.5 StartY=-5 StartZ=0 EndX=57.5 EndY=5 EndZ=0
    g2: LineSegment StartX=57.5 StartY=5 StartZ=0 EndX=42.5 EndY=5 EndZ=0
    g3: LineSegment StartX=42.5 StartY=5 StartZ=0 EndX=42.5 EndY=-5 EndZ=0
    g4: GeomPoint [constr] X=50 Y=0 Z=0
  constraints (12):
    c: Coincident(g0,g1)
    c: Coincident(g1,g2)
    c: Coincident(g2,g3)
    c: Coincident(g3,g0)
    c: Horizontal(g0)
    c: Horizontal(g2)
    c: Vertical(g1)
    c: Vertical(g3)
    c: Symmetric(g2,g0,g4)
    c: Coincident(g4,g-3)
    c: PointOnObject(g2,g-4)
    c: DistanceX(g2,g2) = 15
FEATURE [PartDesign::Pocket] Pocket008
  BaseFeature = -> Pad007
  Direction = (-1,0,0)
  Length = 10
  Length2 = 5
  Profile = -> Sketch018
  ReferenceAxis = -> Sketch018 [N_Axis]
  Refine = true
  SideType = 2
  Suppressed = false
  Type = 0
  Type2 = 0
FEATURE [PartDesign::Chamfer] Chamfer006
  Angle = 45
  Base = -> Pocket008 [Edge9,Edge13]
  BaseFeature = -> Pocket008
  ChamferType = 0
  FlipDirection = false
  Refine = true
  Size = 2
  Size2 = 1
  SupportTransform = false
  Suppressed = false
  UseAllEdges = false
FEATURE [Sketcher::SketchObject] Sketch019
  ArcFitTolerance = 1e-06
  AttachmentSupport = -> [Origin010]
  ExternalTypes = [0]
  FullyConstrained = true
  MakeInternals = false
  MapMode = 5
  Placement = pos=(0,0,0) rot=(1,0,0;1.5708rad)
  sketch-geometry (4):
    g0: ArcOfCircle CenterX=0 CenterY=-5 CenterZ=0 NormalX=0 NormalY=0 NormalZ=1 AngleXU=0 Radius=1.7 StartAngle=3.14159 EndAngle=6.28319
    g1: ArcOfCircle CenterX=0 CenterY=-1.5 CenterZ=0 NormalX=0 NormalY=0 NormalZ=1 AngleXU=0 Radius=1.7 StartAngle=-6.87637e-11 EndAngle=3.14159
    g2: LineSegment StartX=-1.7 StartY=-5 StartZ=0 EndX=-1.7 EndY=-1.5 EndZ=0
    g3: LineSegment StartX=1.7 StartY=-5 StartZ=0 EndX=1.7 EndY=-1.5 EndZ=0
  constraints (10):
    c: Tangent(g0,g2) = 1.5708
    c: Tangent(g0,g3) = -1.5708
    c: Tangent(g1,g2) = 1.5708
    c: Tangent(g1,g3) = -1.5708
    c: Equal(g0,g1)
    c: PointOnObject(g1,g-2)
    c: PointOnObject(g0,g-2)
    c: PointOnObject(g0,g-3)
    c: Distance(g1,g1) = 3.4
    c: DistanceY(g3,g3) = 3.5
FEATURE [PartDesign::Pocket] Pocket009
  BaseFeature = -> Chamfer006
  Direction = (0,1,-2e-16)
  Length = 5
  Length2 = 5
  Profile = -> Sketch019
  ReferenceAxis = -> Sketch019 [N_Axis]
  Refine = true
  SideType = 2
  Suppressed = false
  Type = 1
  Type2 = 0
FEATURE [Sketcher::SketchObject] Sketch020
  ArcFitTolerance = 1e-06
  AttachmentSupport = -> [Origin010]
  ExternalGeometry = -> [Pocket009]
  ExternalTypes = [0,0]
  FullyConstrained = true
  MakeInternals = false
  MapMode = 5
  Placement = pos=(0,0,0) rot=(1,0,0;1.5708rad)
  sketch-geometry (6):
    g0: LineSegment StartX=-1.7 StartY=-5 StartZ=0 EndX=-1.4 EndY=-5 EndZ=0
    g1: LineSegment StartX=-1.7 StartY=-5 StartZ=0 EndX=-1.7 EndY=-4 EndZ=0
    g2: LineSegment StartX=-1.7 StartY=-4 StartZ=0 EndX=-1.4 EndY=-5 EndZ=0
    g3: LineSegment StartX=1.7 StartY=-5 StartZ=0 EndX=1.4 EndY=-5 EndZ=0
    g4: LineSegment StartX=1.4 StartY=-5 StartZ=0 EndX=1.7 EndY=-4 EndZ=0
    g5: LineSegment StartX=1.7 StartY=-4 StartZ=0 EndX=1.7 EndY=-5 EndZ=0
  constraints (16):
    c: Coincident(g0,g-4)
    c: Horizontal(g0)
    c: Coincident(g0,g1)
    c: PointOnObject(g1,g-4)
    c: Coincident(g1,g2)
    c: Coincident(g2,g0)
    c: Coincident(g-3,g3)
    c: Horizontal(g3)
    c: Coincident(g3,g4)
    c: PointOnObject(g4,g-3)
    c: Coincident(g4,g5)
    c: Coincident(g5,g3)
    c: Equal(g3,g0)
    c: Equal(g1,g5)
    c: DistanceX(g0,g3) = 2.8
    c: Distance(g5,g5) = 1
FEATURE [PartDesign::Pad] Pad008
  BaseFeature = -> Pocket009
  Direction = (0,-1,2e-16)
  Length = 5
  Length2 = 10
  Profile = -> Sketch020
  ReferenceAxis = -> Sketch020 [N_Axis]
  Refine = true
  SideType = 2
  Suppressed = false
  Type = 0
  Type2 = 0
FEATURE [PartDesign::Fillet] Fillet007
  Base = -> Pad008 [Edge64,Edge88]
  BaseFeature = -> Pad008
  Radius = 0.2
  Refine = true
  SupportTransform = false
  Suppressed = false
  UseAllEdges = false
FEATURE [PartDesign::LinearPattern] LinearPattern
  BaseFeature = -> Fillet007
  Direction = -> Sketch020 [N_Axis]
  Direction2 = -> Sketch020 [N_Axis]
  Length = 30
  Length2 = 30
  Mode = 0
  Mode2 = 0
  Occurrences = 2
  Occurrences2 = 2
  Offset = 30
  Offset2 = 30
  Originals = -> [Pad008,Fillet007]
  Refine = true
  Reversed2 = true
  SpacingPattern = [0]
  SpacingPattern2 = [0]
  Spacings = [-1]
  Spacings2 = [-1]
  Suppressed = false
  TransformMode = 0
  expr: Length = VarSet.arm_length / 2 - 20 mm
  expr: Length2 = VarSet.arm_length / 2 - 20 mm
FEATURE [PartDesign::Chamfer] Chamfer007
  Angle = 45
  Base = -> LinearPattern [Edge20]
  BaseFeature = -> LinearPattern
  ChamferType = 0
  FlipDirection = false
  Refine = true
  Size = 1
  Size2 = 1
  SupportTransform = false
  Suppressed = false
  UseAllEdges = false
FEATURE [Sketcher::SketchObject] Sketch021
  ArcFitTolerance = 1e-06
  AttachmentSupport = -> [Origin010]
  ExternalGeometry = -> [Chamfer007]
  ExternalTypes = [0,0]
  FullyConstrained = true
  MakeInternals = false
  MapMode = 5
  Placement = pos=(0,0,0) rot=(1,0,0;1.5708rad)
  sketch-geometry (3):
    g0: LineSegment StartX=-8 StartY=5 StartZ=0 EndX=-4 EndY=5 EndZ=0
    g1: LineSegment StartX=-4 StartY=5 StartZ=0 EndX=-8 EndY=1 EndZ=0
    g2: LineSegment StartX=-8 StartY=1 StartZ=0 EndX=-8 EndY=5 EndZ=0
  constraints (8):
    c: Coincident(g-4,g0)
    c: PointOnObject(g0,g-3)
    c: Coincident(g0,g1)
    c: PointOnObject(g1,g-4)
    c: Coincident(g1,g2)
    c: Coincident(g2,g0)
    c: Angle(g1,g2) = 0.785398
    c: DistanceX(g0,g0) = 4
FEATURE [PartDesign::Pocket] Pocket010
  BaseFeature = -> Chamfer007
  Direction = (0,1,-2e-16)
  Length = 80
  Length2 = 5
  Profile = -> Sketch021
  ReferenceAxis = -> Sketch021 [N_Axis]
  Refine = true
  SideType = 2
  Suppressed = false
  Type = 0
  Type2 = 0
  expr: Length = VarSet.arm_length - 20 mm
FEATURE [PartDesign::Draft] Draft
  Angle = 45
  Base = -> Pocket010 [Face38,Face36]
  BaseFeature = -> Pocket010
  Refine = true
  SupportTransform = false
  Suppressed = false
FEATURE [PartDesign::Mirrored] Mirrored002
  BaseFeature = -> Draft
  MirrorPlane = -> Sketch021 [V_Axis]
  Originals = -> [Pocket010,Draft]
  Refine = true
  Suppressed = false
  TransformMode = 0
FEATURE [PartDesign::Chamfer] Chamfer008
  Angle = 45
  Base = -> Mirrored002 [Edge78,Edge128]
  BaseFeature = -> Mirrored002
  ChamferType = 0
  FlipDirection = false
  Refine = true
  Size = 0.6
  Size2 = 1
  SupportTransform = false
  Suppressed = false
  UseAllEdges = false
FEATURE [PartDesign::Chamfer] Chamfer009
  Angle = 45
  Base = -> Chamfer008 [Edge7,Edge50]
  BaseFeature = -> Chamfer008
  ChamferType = 0
  FlipDirection = false
  Refine = true
  Size = 1
  Size2 = 1
  SupportTransform = false
  Suppressed = false
  UseAllEdges = false
FEATURE [PartDesign::Chamfer] Chamfer010
  Angle = 45
  Base = -> Chamfer009 [Edge113,Edge79,Edge80,Edge114]
  BaseFeature = -> Chamfer009
  ChamferType = 0
  FlipDirection = false
  Refine = true
  Size = 0.2
  Size2 = 1
  SupportTransform = false
  Suppressed = false
  UseAllEdges = false
FEATURE [Sketcher::SketchObject] Sketch022
  ArcFitTolerance = 1e-06
  AttachmentSupport = -> [Chamfer010]
  ExternalGeometry = -> [Chamfer010]
  ExternalTypes = [0]
  FullyConstrained = true
  MakeInternals = false
  MapMode = 5
  Placement = pos=(8,0,0) rot=(0.57735,0.57735,0.57735;2.0944rad)
  sketch-geometry (5):
    g0: LineSegment StartX=-57.5 StartY=5 StartZ=0 EndX=-57.5 EndY=-5 EndZ=0
    g1: LineSegment StartX=-57.5 StartY=-5 StartZ=0 EndX=-42.5 EndY=-5 EndZ=0
    g2: LineSegment StartX=-42.5 StartY=-5 StartZ=0 EndX=-42.5 EndY=5 EndZ=0
    g3: LineSegment StartX=-42.5 StartY=5 StartZ=0 EndX=-57.5 EndY=5 EndZ=0
    g4: GeomPoint [constr] X=-50 Y=0 Z=0
  constraints (12):
    c: Coincident(g0,g1)
    c: Coincident(g1,g2)
    c: Coincident(g2,g3)
    c: Coincident(g3,g0)
    c: Vertical(g0)
    c: Vertical(g2)
    c: Horizontal(g1)
    c: Horizontal(g3)
    c: Symmetric(g2,g0,g4)
    c: Coincident(g4,g-3)
    c: Distance(g0,g0) = 10
    c: DistanceX(g3,g3) = 15
FEATURE [PartDesign::Pocket] Pocket011
  BaseFeature = -> Chamfer010
  Direction = (-1,0,0)
  Length = 3
  Length2 = 5
  Profile = -> Sketch022
  ReferenceAxis = -> Sketch022 [N_Axis]
  Refine = true
  SideType = 0
  Suppressed = false
  Type = 0
  Type2 = 0
FEATURE [PartDesign::Mirrored] Mirrored003
  BaseFeature = -> Pocket011
  MirrorPlane = -> YZ_Plane005
  Originals = -> [Pocket011]
  Refine = true
  Suppressed = false
  TransformMode = 0
FEATURE [PartDesign::Chamfer] Chamfer011
  Angle = 45
  Base = -> Mirrored003 [Edge82,Edge12,Edge156,Edge45]
  BaseFeature = -> Mirrored003
  ChamferType = 0
  FlipDirection = false
  Refine = true
  Size = 2
  Size2 = 1
  SupportTransform = false
  Suppressed = false
  UseAllEdges = false
FEATURE [PartDesign::Chamfer] Chamfer012
  Angle = 45
  Base = -> Chamfer011 [Edge89,Edge70]
  BaseFeature = -> Chamfer011
  ChamferType = 0
  FlipDirection = false
  Refine = true
  Size = 0.6
  Size2 = 1
  SupportTransform = false
  Suppressed = false
  UseAllEdges = false
FEATURE [PartDesign::Body] Body004  label="Arm"
  AllowCompound = true
  Group = -> [Sketch017,Pad007,Sketch018,Pocket008,Chamfer006,Sketch019,Pocket009,Sketch020,Pad008,Fillet007,LinearPattern,Chamfer007,Sketch021,Pocket010,Draft,Mirrored002,Chamfer008,Chamfer009,Chamfer010,Sketch022,Pocket011,Mirrored003,Chamfer011,Chamfer012]
  Origin = -> Origin010
  Placement = pos=(-7.1e-15,-96.8,3) rot=(0,0,1;0rad)
  Tip = -> Chamfer012
FEATURE [App::Point] Origin013  label="Origine012"
  Role = Origin
FEATURE [Sketcher::SketchObject] Sketch023
  ArcFitTolerance = 1e-06
  AttachmentSupport = -> [Origin012]
  ExternalTypes = [0]
  FullyConstrained = true
  MakeInternals = false
  MapMode = 5
  Placement = pos=(0,0,0) rot=(0.57735,0.57735,0.57735;2.0944rad)
  sketch-geometry (12):
    g0: Circle CenterX=0 CenterY=0 CenterZ=0 NormalX=0 NormalY=0 NormalZ=1 AngleXU=0 Radius=1.7
    g1: ArcOfCircle CenterX=0 CenterY=0 CenterZ=0 NormalX=0 NormalY=0 NormalZ=1 AngleXU=0 Radius=5 StartAngle=0 EndAngle=1.5708
    g2: LineSegment StartX=5 StartY=0 StartZ=0 EndX=5 EndY=-5 EndZ=0
    g3: LineSegment [constr] StartX=5 StartY=-5 StartZ=0 EndX=-32 EndY=-5 EndZ=0
    g4: LineSegment [constr] StartX=-32 StartY=-5 StartZ=0 EndX=-32 EndY=5 EndZ=0
    g5: LineSegment [constr] StartX=-32 StartY=5 StartZ=0 EndX=0 EndY=5 EndZ=0
    g6: LineSegment [constr] StartX=-12 StartY=5 StartZ=0 EndX=-12 EndY=-5 EndZ=0
    g7: LineSegment StartX=5 StartY=-5 StartZ=0 EndX=-32 EndY=-5 EndZ=0
    g8: LineSegment StartX=-32 StartY=-5 StartZ=0 EndX=-32 EndY=2 EndZ=0
    g9: LineSegment StartX=-32 StartY=2 StartZ=0 EndX=-12 EndY=2 EndZ=0
    g10: LineSegment StartX=-12 StartY=2 StartZ=0 EndX=-12 EndY=5 EndZ=0
    g11: LineSegment StartX=-12 StartY=5 StartZ=0 EndX=0 EndY=5 EndZ=0
  constraints (30):
    c: Coincident(g0,g-1)
    c: Diameter(g0) = 3.4
    c: Coincident(g1,g0)
    c: PointOnObject(g1,g-1)
    c: PointOnObject(g1,g-2)
    c: Tangent(g1,g2) = 1.5708
    c: Coincident(g2,g3)
    c: Horizontal(g3)
    c: Coincident(g3,g4)
    c: Coincident(g4,g5)
    c: Coincident(g5,g1)
    c: Horizontal(g5)
    c: Symmetric(g3,g4,g-1)
    c: Distance(g4,g4) = 10
    c: Vertical(g6)
    c: Distance(g0,g6) = 12
    c: PointOnObject(g6,g3)
    c: Distance(g6,g4) = 20
    c: Coincident(g7,g2)
    c: Coincident(g7,g3)
    c: Coincident(g8,g3)
    c: PointOnObject(g8,g4)
    c: Coincident(g9,g8)
    c: PointOnObject(g9,g6)
    c: Horizontal(g9)
    c: Coincident(g10,g9)
    c: Coincident(g10,g6)
    c: Coincident(g11,g6)
    c: Tangent(g11,g1) = 1.5708
    c: DistanceY(g8,g8) = 7
FEATURE [PartDesign::Pad] Pad009
  Direction = (1,0,0)
  Length = 16
  Length2 = 10
  Profile = -> Sketch023
  ReferenceAxis = -> Sketch023 [N_Axis]
  Refine = true
  SideType = 2
  Suppressed = false
  Type = 0
  Type2 = 0
FEATURE [Sketcher::SketchObject] Sketch024
  ArcFitTolerance = 1e-06
  AttachmentSupport = -> [Origin012]
  ExternalTypes = [0]
  FullyConstrained = true
  MakeInternals = false
  MapMode = 5
  Placement = pos=(0,0,0) rot=(0.57735,0.57735,0.57735;2.0944rad)
  sketch-geometry (5):
    g0: LineSegment StartX=-7.5 StartY=-5 StartZ=0 EndX=7.5 EndY=-5 EndZ=0
    g1: LineSegment StartX=7.5 StartY=-5 StartZ=0 EndX=7.5 EndY=5 EndZ=0
    g2: LineSegment StartX=7.5 StartY=5 StartZ=0 EndX=-7.5 EndY=5 EndZ=0
    g3: LineSegment StartX=-7.5 StartY=5 StartZ=0 EndX=-7.5 EndY=-5 EndZ=0
    g4: GeomPoint [constr] X=0 Y=0 Z=0
  constraints (12):
    c: Coincident(g0,g1)
    c: Coincident(g1,g2)
    c: Coincident(g2,g3)
    c: Coincident(g3,g0)
    c: Horizontal(g0)
    c: Horizontal(g2)
    c: Vertical(g1)
    c: Vertical(g3)
    c: Symmetric(g2,g0,g4)
    c: Coincident(g4,g-1)
    c: DistanceX(g2,g2) = 15
    c: DistanceY(g1,g1) = 10
FEATURE [PartDesign::Pocket] Pocket012
  BaseFeature = -> Pad009
  Direction = (-1,0,0)
  Length = 10
  Length2 = 5
  Profile = -> Sketch024
  ReferenceAxis = -> Sketch024 [N_Axis]
  Refine = true
  SideType = 2
  Suppressed = false
  Type = 0
  Type2 = 0
FEATURE [PartDesign::Chamfer] Chamfer013
  Angle = 45
  Base = -> Pocket012 [Edge22,Edge30]
  BaseFeature = -> Pocket012
  ChamferType = 0
  FlipDirection = false
  Refine = true
  Size = 2
  Size2 = 1
  SupportTransform = false
  Suppressed = false
  UseAllEdges = false
FEATURE [Sketcher::SketchObject] Sketch025
  ArcFitTolerance = 1e-06
  AttachmentSupport = -> [Chamfer013]
  ExternalTypes = [0]
  FullyConstrained = true
  MakeInternals = false
  MapMode = 5
  Placement = pos=(0,0,2) rot=(0,0,1;0rad)
  sketch-geometry (1):
    g0: Circle CenterX=0 CenterY=-22 CenterZ=0 NormalX=0 NormalY=0 NormalZ=1 AngleXU=0 Radius=2.7
  constraints (3):
    c: PointOnObject(g0,g-2)
    c: Diameter(g0) = 5.4
    c: Distance(g0,g-3) = 10
FEATURE [PartDesign::Pocket] Pocket013
  BaseFeature = -> Chamfer013
  Direction = (0,0,-1)
  Length = 5
  Length2 = 5
  Profile = -> Sketch025
  ReferenceAxis = -> Sketch025 [N_Axis]
  Refine = true
  SideType = 0
  Suppressed = false
  Type = 1
  Type2 = 0
FEATURE [PartDesign::Chamfer] Chamfer014
  Angle = 45
  Base = -> Pocket013 [Edge3,Edge21]
  BaseFeature = -> Pocket013
  ChamferType = 0
  FlipDirection = false
  Refine = true
  Size = 1
  Size2 = 1
  SupportTransform = false
  Suppressed = false
  UseAllEdges = false
FEATURE [PartDesign::Chamfer] Chamfer015
  Angle = 45
  Base = -> Chamfer014 [Edge45,Edge43]
  BaseFeature = -> Chamfer014
  ChamferType = 0
  FlipDirection = false
  Refine = true
  Size = 1
  Size2 = 1
  SupportTransform = false
  Suppressed = false
  UseAllEdges = false
FEATURE [PartDesign::Chamfer] Chamfer016
  Angle = 45
  Base = -> Chamfer015 [Edge29,Edge50]
  BaseFeature = -> Chamfer015
  ChamferType = 0
  FlipDirection = false
  Refine = true
  Size = 2
  Size2 = 1
  SupportTransform = false
  Suppressed = false
  UseAllEdges = false
FEATURE [PartDesign::Chamfer] Chamfer017
  Angle = 45
  Base = -> Chamfer016 [Edge33,Edge49]
  BaseFeature = -> Chamfer016
  ChamferType = 0
  FlipDirection = false
  Refine = true
  Size = 1
  Size2 = 1
  SupportTransform = false
  Suppressed = false
  UseAllEdges = false
FEATURE [PartDesign::Chamfer] Chamfer018
  Angle = 45
  Base = -> Chamfer017 [Edge69,Edge63,Edge34,Edge27]
  BaseFeature = -> Chamfer017
  ChamferType = 0
  FlipDirection = false
  Refine = true
  Size = 0.4
  Size2 = 1
  SupportTransform = false
  Suppressed = false
  UseAllEdges = false
FEATURE [PartDesign::Body] Body005  label="2020-Support"
  AllowCompound = true
  Group = -> [Sketch023,Pad009,Sketch024,Pocket012,Chamfer013,Sketch025,Pocket013,Chamfer014,Chamfer015,Chamfer016,Chamfer017,Chamfer018]
  Origin = -> Origin012
  Tip = -> Chamfer018
FEATURE [App::Point] Origin015  label="Origine014"
  Role = Origin
FEATURE [Sketcher::SketchObject] Sketch026
  ArcFitTolerance = 1e-06
  AttachmentSupport = -> [Origin014]
  ExternalTypes = [0]
  FullyConstrained = true
  MakeInternals = false
  MapMode = 5
  Placement = pos=(0,0,0) rot=(0.57735,0.57735,0.57735;2.0944rad)
  sketch-geometry (2):
    g0: Circle CenterX=0 CenterY=0 CenterZ=0 NormalX=0 NormalY=0 NormalZ=1 AngleXU=0 Radius=7.5
    g1: Circle CenterX=0 CenterY=0 CenterZ=0 NormalX=0 NormalY=0 NormalZ=1 AngleXU=0 Radius=1.7
  constraints (4):
    c: Coincident(g0,g-1)
    c: Diameter(g0) = 15
    c: Coincident(g1,g0)
    c: Diameter(g1) = 3.4
FEATURE [PartDesign::Pad] Pad010
  Direction = (1,0,0)
  Length = 7
  Length2 = 10
  Profile = -> Sketch026
  ReferenceAxis = -> Sketch026 [N_Axis]
  Refine = true
  SideType = 2
  Suppressed = false
  Type = 0
  Type2 = 0
FEATURE [Sketcher::SketchObject] Sketch027
  ArcFitTolerance = 1e-06
  AttachmentSupport = -> [Pad010]
  ExternalTypes = [0]
  FullyConstrained = true
  MakeInternals = false
  MapMode = 5
  Placement = pos=(3.5,0,0) rot=(0.57735,0.57735,0.57735;2.0944rad)
  sketch-geometry (7):
    g0: LineSegment StartX=3.23316 StartY=0 StartZ=0 EndX=1.61658 EndY=2.8 EndZ=0
    g1: LineSegment StartX=1.61658 StartY=2.8 StartZ=0 EndX=-1.61658 EndY=2.8 EndZ=0
    g2: LineSegment StartX=-1.61658 StartY=2.8 StartZ=0 EndX=-3.23316 EndY=0 EndZ=0
    g3: LineSegment StartX=-3.23316 StartY=0 StartZ=0 EndX=-1.61658 EndY=-2.8 EndZ=0
    g4: LineSegment StartX=-1.61658 StartY=-2.8 StartZ=0 EndX=1.61658 EndY=-2.8 EndZ=0
    g5: LineSegment StartX=1.61658 StartY=-2.8 StartZ=0 EndX=3.23316 EndY=0 EndZ=0
    g6: Circle [constr] CenterX=0 CenterY=0 CenterZ=0 NormalX=0 NormalY=0 NormalZ=1 AngleXU=0 Radius=3.23316
  constraints (16):
    c: Coincident(g0,g1)
    c: Coincident(g1,g2)
    c: Coincident(g2,g3)
    c: Coincident(g3,g4)
    c: Coincident(g4,g5)
    c: Coincident(g5,g0)
    c: Equal(g0, g1-g5) x5
    c: PointOnObject(g0,g6)
    c: PointOnObject(g1,g6)
    c: PointOnObject(g2,g6)
    c: PointOnObject(g3,g6)
    c: PointOnObject(g4,g6)
    c: PointOnObject(g5,g6)
    c: Coincident(g6,g-1)
    c: PointOnObject(g5,g-1)
    c: Distance(g4,g1) = 5.6
FEATURE [PartDesign::Pocket] Pocket014
  BaseFeature = -> Pad010
  Direction = (-1,0,0)
  Length = 3
  Length2 = 5
  Profile = -> Sketch027
  ReferenceAxis = -> Sketch027 [N_Axis]
  Refine = true
  SideType = 0
  Suppressed = false
  Type = 0
  Type2 = 0
FEATURE [PartDesign::Chamfer] Chamfer019
  Angle = 45
  Base = -> Pocket014 [Edge4,Edge12]
  BaseFeature = -> Pocket014
  ChamferType = 0
  FlipDirection = false
  Refine = true
  Size = 0.4
  Size2 = 1
  SupportTransform = false
  Suppressed = false
  UseAllEdges = false
FEATURE [PartDesign::Chamfer] Chamfer020
  Angle = 45
  Base = -> Chamfer019 [Edge2,Edge6]
  BaseFeature = -> Chamfer019
  ChamferType = 0
  FlipDirection = false
  Refine = true
  Size = 1
  Size2 = 1
  SupportTransform = false
  Suppressed = false
  UseAllEdges = false
FEATURE [Sketcher::SketchObject] Sketch028
  ArcFitTolerance = 1e-06
  AttachmentSupport = -> [Origin014]
  ExternalGeometry = -> [Chamfer020]
  ExternalTypes = [0]
  FullyConstrained = true
  MakeInternals = false
  MapMode = 5
  Placement = pos=(0,0,0) rot=(0.57735,0.57735,0.57735;2.0944rad)
  sketch-geometry (4):
    g0: LineSegment StartX=0 StartY=6.5 StartZ=0 EndX=0.866025 EndY=8 EndZ=0
    g1: LineSegment StartX=0.866025 StartY=8 StartZ=0 EndX=-0.866025 EndY=8 EndZ=0
    g2: LineSegment StartX=-0.866025 StartY=8 StartZ=0 EndX=0 EndY=6.5 EndZ=0
    g3: Circle [constr] CenterX=0 CenterY=7.5 CenterZ=0 NormalX=0 NormalY=0 NormalZ=1 AngleXU=0 Radius=1
  constraints (12):
    c: Coincident(g0,g1)
    c: Coincident(g1,g2)
    c: Coincident(g2,g0)
    c: Equal(g0,g1)
    c: Equal(g0,g2)
    c: PointOnObject(g0,g3)
    c: PointOnObject(g1,g3)
    c: PointOnObject(g2,g3)
    c: PointOnObject(g3,g-2)
    c: PointOnObject(g2,g-2)
    c: PointOnObject(g3,g-3)
    c: Distance(g0,g3) = 1
FEATURE [PartDesign::Pocket] Pocket015
  BaseFeature = -> Chamfer020
  Direction = (-1,0,0)
  Length = 7
  Length2 = 5
  Profile = -> Sketch028
  ReferenceAxis = -> Sketch028 [N_Axis]
  Refine = true
  SideType = 2
  Suppressed = false
  Type = 0
  Type2 = 0
FEATURE [PartDesign::PolarPattern] PolarPattern
  Angle = 360
  Axis = -> Sketch028 [N_Axis]
  BaseFeature = -> Pocket015
  Mode = 0
  Occurrences = 20
  Offset = 120
  Originals = -> [Pocket015]
  Refine = true
  SpacingPattern = [0]
  Spacings = [-1,-1,-1,-1,-1,-1,-1,-1,-1,-1,-1,-1,-1,-1,-1,-1,-1,-1,-1]
  Suppressed = false
  TransformMode = 0
FEATURE [PartDesign::Chamfer] Chamfer021
  Angle = 45
  Base = -> PolarPattern [Edge229,Edge230,Edge231,Edge232,Edge233,Edge228]
  BaseFeature = -> PolarPattern
  ChamferType = 0
  FlipDirection = false
  Refine = true
  Size = 0.4
  Size2 = 1
  SupportTransform = false
  Suppressed = false
  UseAllEdges = false
FEATURE [PartDesign::Body] Body006  label="Knurling-Nut"
  AllowCompound = true
  Group = -> [Sketch026,Pad010,Sketch027,Pocket014,Chamfer019,Chamfer020,Sketch028,Pocket015,PolarPattern,Chamfer021]
  Origin = -> Origin014
  Placement = pos=(-11.5,0,0) rot=(0,0,1;0rad)
  Tip = -> Chamfer021
FEATURE [App::Point] Origin017  label="Origine016"
  Role = Origin
FEATURE [App::Link] Link  label="Knurling-Nut001"
  LinkPlacement = pos=(11.5,0,0) rot=(0,0,1;0rad)
  LinkedObject = -> Body006
  Placement = pos=(11.5,0,0) rot=(0,0,1;0rad)
FEATURE [Part::FeaturePython] Screw  label="M3x30-Vis"  # WARN: FeaturePython — macro-defined, semantics opaque (R4)
  BaseObject = -> Body006 [Chamfer021.Edge254]
  Diameter = 1
  Invert = true
  LeftHanded = false
  Length = 8
  LengthCustom = 30
  MatchOuter = false
  OffsetAngle = 0
  Placement = pos=(-15,0,0) rot=(0,-1,0;1.5708rad)
  Thread = false
  Type = 85
FEATURE [Part::FeaturePython] Nut  label="M3-Écrou"  # WARN: FeaturePython — macro-defined, semantics opaque (R4)
  BaseObject = -> Body006 [Chamfer021.Edge231]
  Diameter = 4
  Invert = true
  LeftHanded = false
  MatchOuter = false
  OffsetAngle = 30
  Placement = pos=(-11,0,0) rot=(0.250563,0.935113,0.250563;1.63783rad)
  Thread = false
  Type = 31
FEATURE [Part::FeaturePython] Nut001  label="M3-Écrou001"  # WARN: FeaturePython — macro-defined, semantics opaque (R4)
  BaseObject = -> Link [Chamfer021.Edge231]
  Diameter = 4
  Invert = true
  LeftHanded = false
  MatchOuter = false
  OffsetAngle = 30
  Placement = pos=(12,0,0) rot=(0.250563,0.935113,0.250563;1.63783rad)
  Thread = false
  Type = 31
FEATURE [App::DocumentObjectGroup] Group  label="Fasteners-Knurling-Nut"
  Group = -> [Screw,Nut,Nut001]
FEATURE [App::Part] Part001  label="Knurling-Nut-Asm"
  Group = -> [Body006,Link,Group,Screw,Nut,Nut001]
  Origin = -> Origin016
  Placement = pos=(-7.1e-15,-46.8,3) rot=(0,0,1;0rad)
FEATURE [App::Point] Origin019  label="Origine018"
  Role = Origin
FEATURE [Part::FeaturePython] Screw001  label="M5x12-Vis"  # WARN: FeaturePython — macro-defined, semantics opaque (R4)
  BaseObject = -> Body005 [Chamfer018.Edge42]
  Diameter = 3
  Invert = true
  LeftHanded = false
  Length = 2
  LengthCustom = 12
  MatchOuter = true
  OffsetAngle = 0
  Placement = pos=(0,-22,-5) rot=(-1,0,0;3.14159rad)
  Thread = false
  Type = 85
FEATURE [Part::FeaturePython] TSlot  label="M5 x 20 series-TSlot"  # WARN: FeaturePython — macro-defined, semantics opaque (R4)
  BaseObject = -> Body005 [Chamfer018.Edge28]
  Diameter = 3
  Invert = true
  LeftHanded = false
  MatchOuter = true
  OffsetAngle = 0
  Placement = pos=(0,-22,2) rot=(-1,0,0;3.14159rad)
  SlotWidth = 0
  Thread = false
  Type = 1
FEATURE [App::DocumentObjectGroup] Group001  label="Fasteners-Support"
  Group = -> [Screw001,TSlot]
FEATURE [App::Part] Part002  label="2020-Support-Asm"
  Group = -> [Body005,Group001,Screw001,TSlot]
  Origin = -> Origin018
  Placement = pos=(-7.1e-15,-146.8,3) rot=(0,0,1;0rad)
FEATURE [App::VarSet] VarSet
  arm_length = 100
